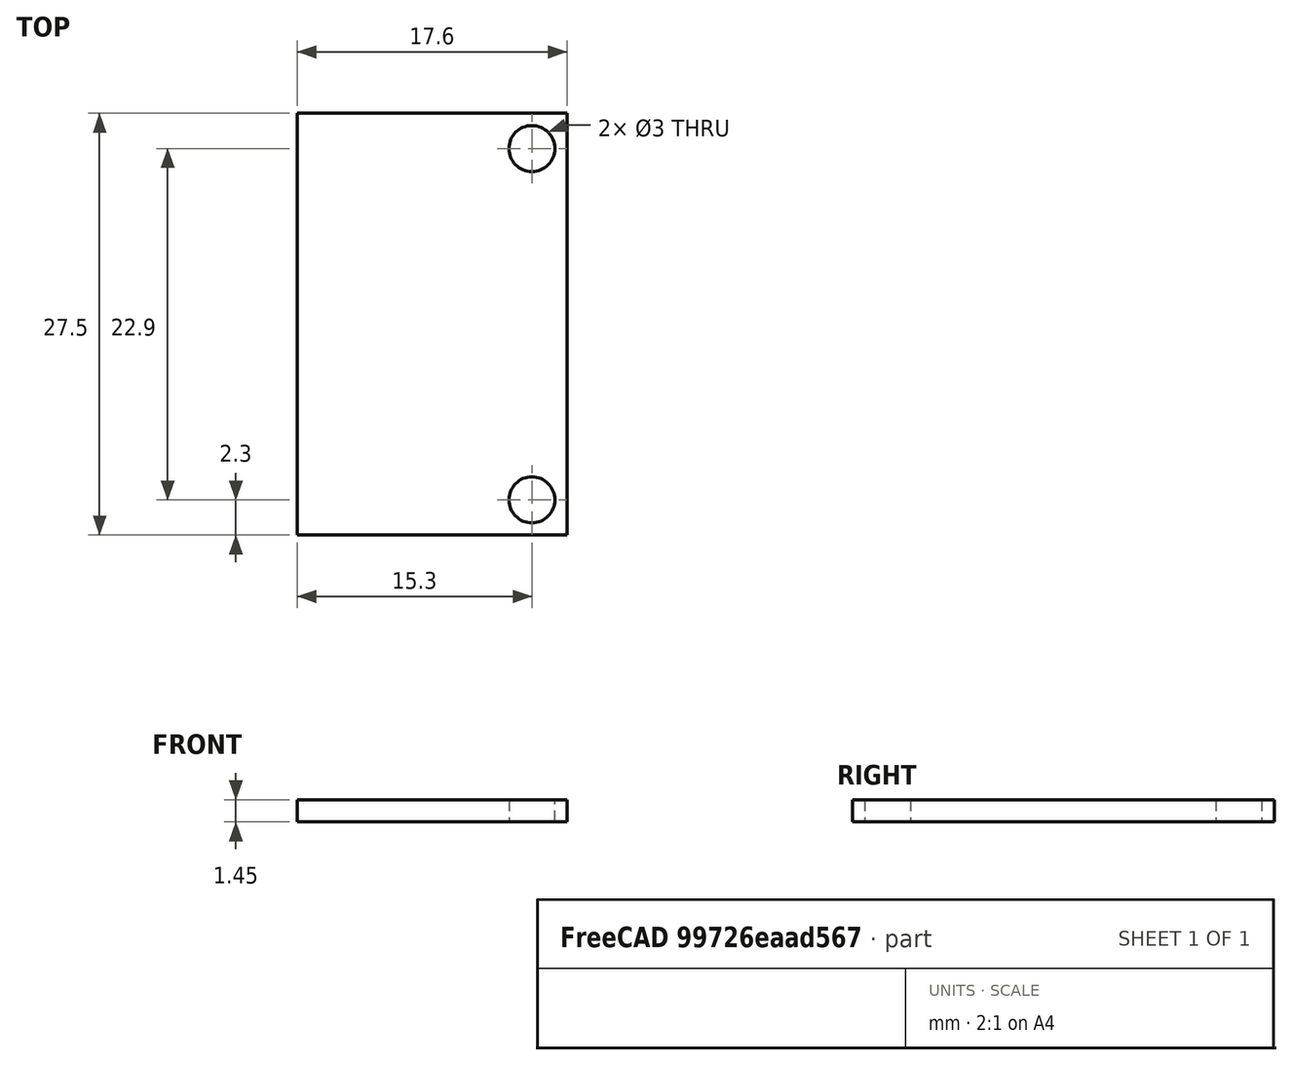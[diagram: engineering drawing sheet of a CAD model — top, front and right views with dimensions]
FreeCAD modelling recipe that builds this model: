
FCSTD DOCUMENT  (FreeCAD 0.20R29177 (Git))
Label: ads1115
License: All rights reserved
LicenseURL: http://en.wikipedia.org/wiki/All_rights_reserved
objects: Sketcher::SketchObject×1, PartDesign::Pad×1, PartDesign::Body×1
note: 4 computed .brp shape members not serialized (recipe doc carries the construction recipe); baked Part::Feature solids carry a one-line shape summary decoded from their .brp

FEATURE [Sketcher::SketchObject] Sketch
  FullyConstrained = true
  expr: Constraints[13] = .Constraints.bohr_radius / 2 + 0.8mm
  expr: Constraints[14] = .Constraints.bohr_radius / 2 + 0.8mm
  expr: Constraints[15] = .Constraints.bohr_radius / 2 + 0.8mm
  expr: Constraints[16] = .Constraints.bohr_radius / 2 + 0.8mm
  sketch-geometry (6):
    g0: LineSegment StartX=-8.8 StartY=13.75 StartZ=0 EndX=8.8 EndY=13.75 EndZ=0
    g1: LineSegment StartX=8.8 StartY=13.75 StartZ=0 EndX=8.8 EndY=-13.75 EndZ=0
    g2: LineSegment StartX=8.8 StartY=-13.75 StartZ=0 EndX=-8.8 EndY=-13.75 EndZ=0
    g3: LineSegment StartX=-8.8 StartY=-13.75 StartZ=0 EndX=-8.8 EndY=13.75 EndZ=0
    g4: Circle CenterX=6.5 CenterY=11.45 CenterZ=0 NormalX=0 NormalY=0 NormalZ=1 AngleXU=0 Radius=1.5
    g5: Circle CenterX=6.5 CenterY=-11.45 CenterZ=0 NormalX=0 NormalY=0 NormalZ=1 AngleXU=0 Radius=1.5
  constraints (17):
    c: Coincident(g0,g1)
    c: Coincident(g1,g2)
    c: Coincident(g2,g3)
    c: Coincident(g3,g0)
    c: Horizontal(g0)
    c: Horizontal(g2)
    c: Vertical(g1)
    c: Vertical(g3)
    c: Symmetric(g2,g0,g-1)
    c: DistanceX(g0,g0) = 17.6  'breite'
    c: DistanceY(g1,g1) = 27.5  'hoehe'
    c: Equal(g4,g5)
    c: Diameter(g4) = 3  'bohr_radius'
    c: DistanceY(g4,g0) = 2.3
    c: DistanceX(g4,g0) = 2.3
    c: DistanceX(g5,g1) = 2.3
    c: DistanceY(g1,g5) = 2.3
FEATURE [PartDesign::Pad] Pad
  Direction = (0,0,1)
  Length = 1.45
  Length2 = 10
  Profile = -> Sketch
  ReferenceAxis = -> Sketch [N_Axis]
  Type = 0
FEATURE [PartDesign::Body] Body
  Group = -> [Sketch,Pad]
  Origin = -> Origin
  Tip = -> Pad
